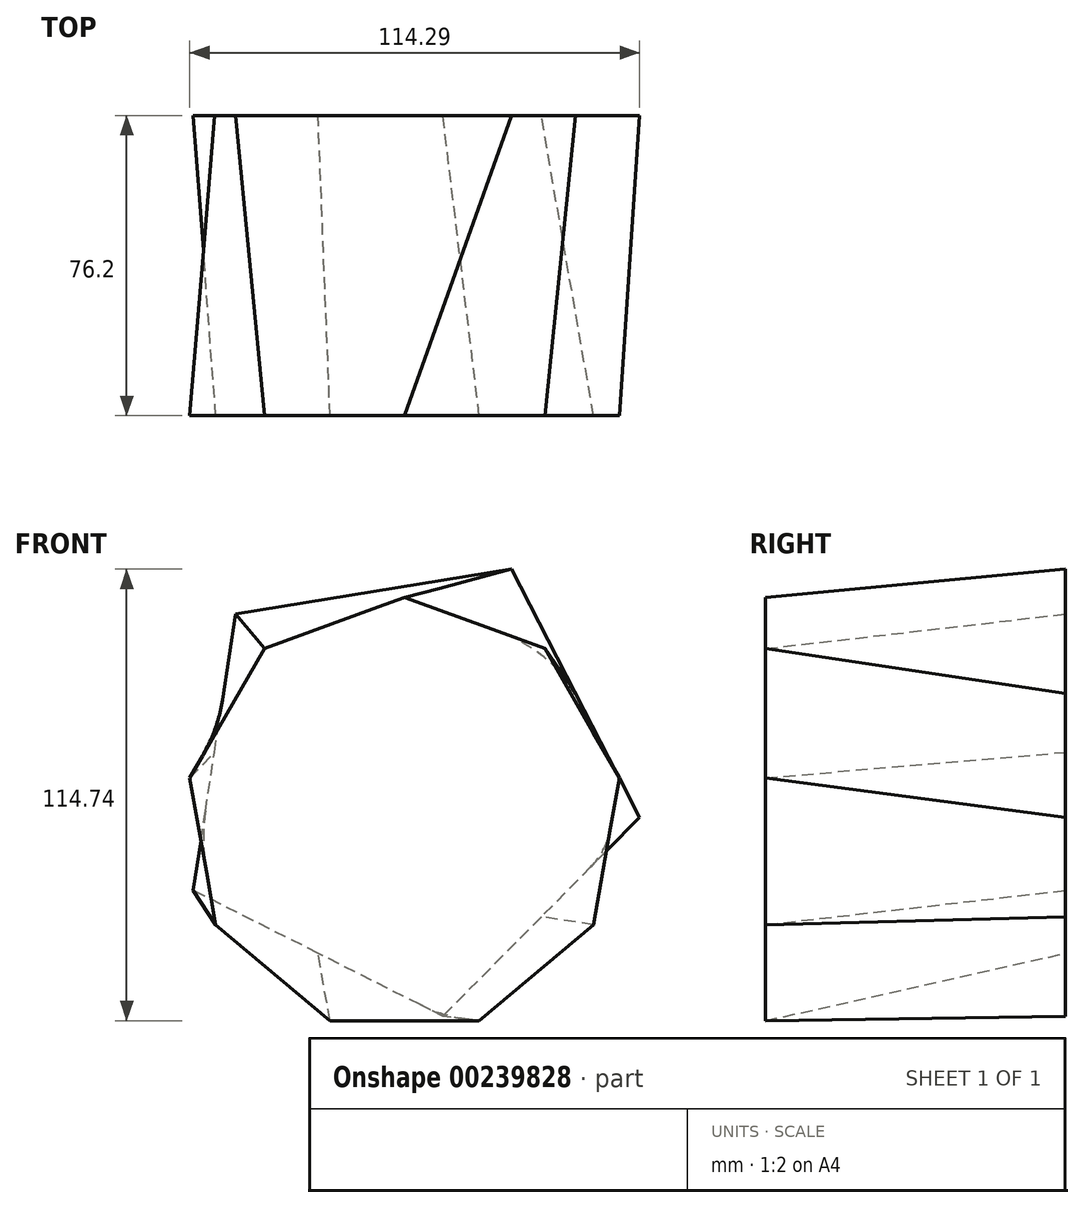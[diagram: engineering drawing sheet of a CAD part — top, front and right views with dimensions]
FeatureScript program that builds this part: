
annotation { "Feature Type Name" : "Feature", "Feature Type Description" : "" }
export const myFeature = defineFeature(function(context is Context, id is Id, definition is map)
    precondition{}
    {
        {
            var Q0;
            Q0=qCreatedBy(makeId("Front.planeOp"),FACE);
            var sketch = newSketch(context, id + "F0", { "sketchPlane" : qUnion([Q0])});
            skCircle(sketch, "E0.cCircle", {"center": v(0, 3.74) * mm, "radius": 48.89 * mm, "construction": true});
            skLineSegment(sketch, "E0.0", {"start": v(9.72, -55.9) * mm, "end": v(-53.72, -23.93) * mm});
            skLineSegment(sketch, "E0.1", {"start": v(-53.72, -23.93) * mm, "end": v(-42.92, 46.28) * mm});
            skLineSegment(sketch, "E0.2", {"start": v(-42.92, 46.28) * mm, "end": v(27.2, 57.7) * mm});
            skLineSegment(sketch, "E0.3", {"start": v(27.2, 57.7) * mm, "end": v(59.72, -5.44) * mm});
            skLineSegment(sketch, "E0.4", {"start": v(59.72, -5.44) * mm, "end": v(9.72, -55.9) * mm});
            skPoint(sketch, "E0.0.midPoint", {"position": v(-22, -39.91) * mm});
            skSolve(sketch);
        }
        {
            var Q0;
            Q0=qCreatedBy(makeId("Front.planeOp"),FACE);
            cPlane(context, id + "F1", {"entities" : qUnion([Q0]), "cplaneType" : CPlaneType.OFFSET, "offset" : 76.2 * mm, "width" : 152.4 * mm, "height" : 152.4 * mm});
        }
        {
            var Q0;
            Q0=qCreatedBy(id+"F1.planeOp",FACE);
            var sketch = newSketch(context, id + "F2", { "sketchPlane" : qUnion([Q0])});
            skCircle(sketch, "E1.cCircle", {"center": v(0, -4.95) * mm, "radius": 52.07 * mm, "construction": true});
            skLineSegment(sketch, "E1.0", {"start": v(18.95, -57.03) * mm, "end": v(-18.95, -57.03) * mm});
            skLineSegment(sketch, "E1.1", {"start": v(-18.95, -57.03) * mm, "end": v(-48, -32.66) * mm});
            skLineSegment(sketch, "E1.2", {"start": v(-48, -32.66) * mm, "end": v(-54.57, 4.67) * mm});
            skLineSegment(sketch, "E1.3", {"start": v(-54.57, 4.67) * mm, "end": v(-35.62, 37.5) * mm});
            skLineSegment(sketch, "E1.4", {"start": v(-35.62, 37.5) * mm, "end": v(0, 50.46) * mm});
            skLineSegment(sketch, "E1.5", {"start": v(0, 50.46) * mm, "end": v(35.62, 37.5) * mm});
            skLineSegment(sketch, "E1.6", {"start": v(35.62, 37.5) * mm, "end": v(54.57, 4.67) * mm});
            skLineSegment(sketch, "E1.7", {"start": v(54.57, 4.67) * mm, "end": v(48, -32.66) * mm});
            skLineSegment(sketch, "E1.8", {"start": v(48, -32.66) * mm, "end": v(18.95, -57.03) * mm});
            skPoint(sketch, "E1.0.midPoint", {"position": v(0, -57.03) * mm});
            skSolve(sketch);
        }
        {
            var Q0;
            Q0=makeQuery(id+"F2.imprint","IMPRINT",FACE,{"disambiguationData":[TD([[makeQuery(id+"F2.imprint","IMPRINT",EDGE,{"derivedFrom":sQuery(id+"F2.wireOp",EDGE,"E1.0")}),-1.0]])]});
            var Q1;
            Q1=makeQuery(id+"F0.imprint","IMPRINT",FACE,{"disambiguationData":[TD([[makeQuery(id+"F0.imprint","IMPRINT",EDGE,{"derivedFrom":sQuery(id+"F0.wireOp",EDGE,"E0.0")}),-1.0]])]});
            loft(context, id + "F3", {"sheetProfilesArray" : [{ "sheetProfileEntities" : qUnion([Q0]) }, { "sheetProfileEntities" : qUnion([Q1]) }]});
        }
    });
